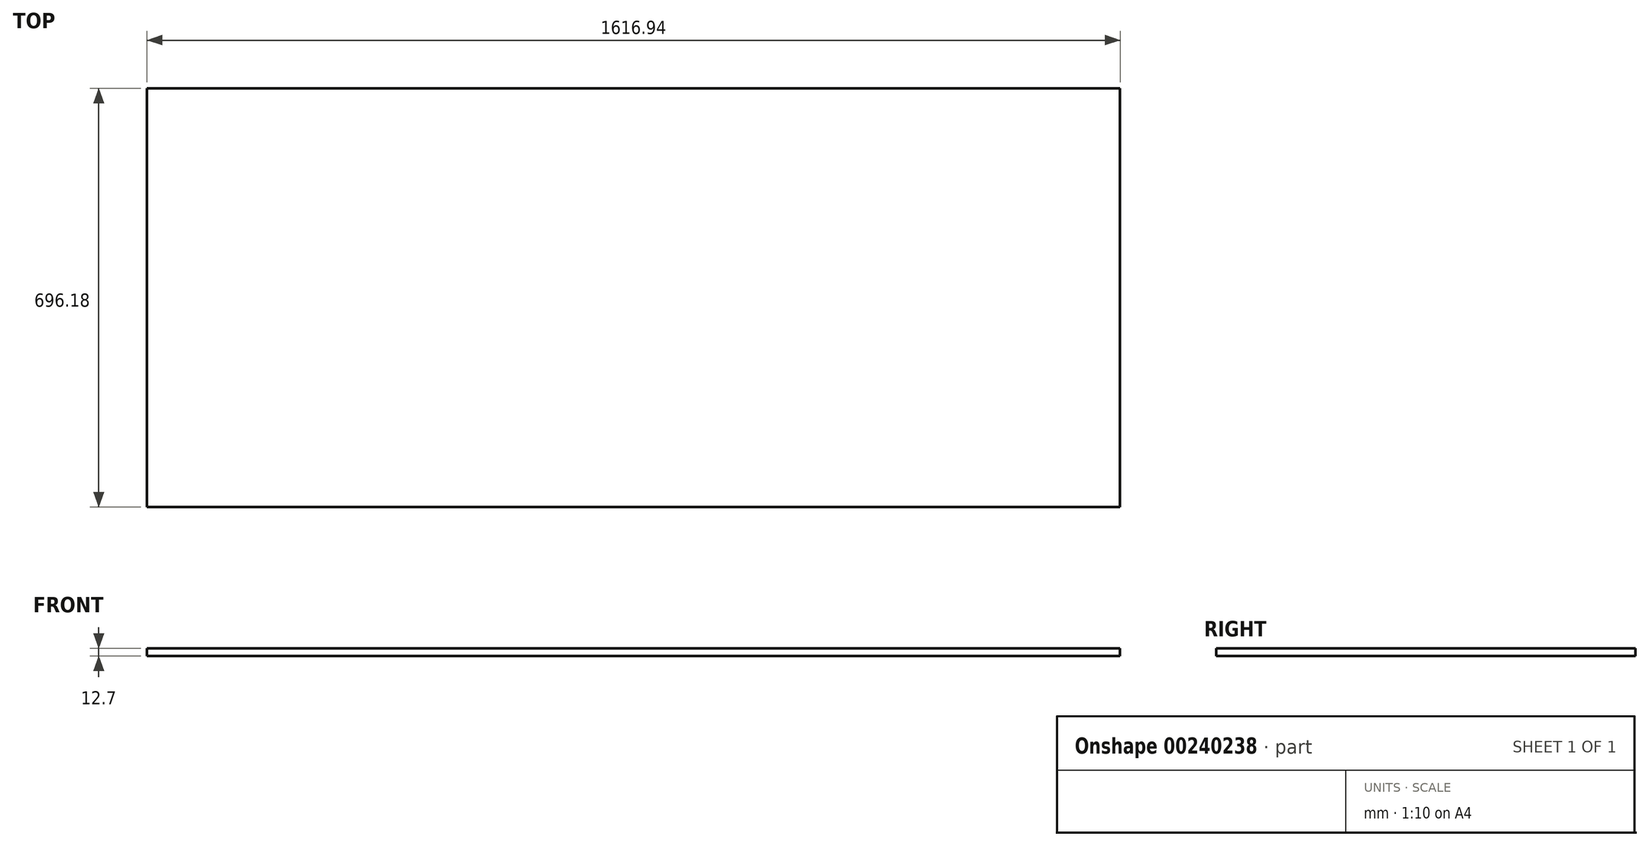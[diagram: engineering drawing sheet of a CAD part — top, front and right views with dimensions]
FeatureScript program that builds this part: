
annotation { "Feature Type Name" : "Feature", "Feature Type Description" : "" }
export const myFeature = defineFeature(function(context is Context, id is Id, definition is map)
    precondition{}
    {
        {
            var Q0;
            Q0=qCreatedBy(makeId("Top.planeOp"),FACE);
            var sketch = newSketch(context, id + "F0", { "sketchPlane" : qUnion([Q0])});
            skLineSegment(sketch, "E0.bottom", {"start": v(808.47, -348.1) * mm, "end": v(-808.47, -348.1) * mm});
            skLineSegment(sketch, "E0.top", {"start": v(808.47, 348.1) * mm, "end": v(-808.47, 348.1) * mm});
            skLineSegment(sketch, "E0.left", {"start": v(808.47, -348.1) * mm, "end": v(808.47, 348.1) * mm});
            skLineSegment(sketch, "E0.right", {"start": v(-808.47, -348.1) * mm, "end": v(-808.47, 348.1) * mm});
            skPoint(sketch, "E0.middle", {"position": v(0, 0) * mm});
            skLineSegment(sketch, "E1", {"start": v(0, 348.1) * mm, "end": v(0, -348.1) * mm, "construction": true});
            skLineSegment(sketch, "E2", {"start": v(-808.47, 0) * mm, "end": v(808.47, 0) * mm, "construction": true});
            skLineSegment(sketch, "E3.bottom", {"start": v(76.2, -76.2) * mm, "end": v(-76.2, -76.2) * mm, "construction": true});
            skLineSegment(sketch, "E3.top", {"start": v(76.2, 76.2) * mm, "end": v(-76.2, 76.2) * mm, "construction": true});
            skLineSegment(sketch, "E3.left", {"start": v(76.2, -76.2) * mm, "end": v(76.2, 76.2) * mm, "construction": true});
            skLineSegment(sketch, "E3.right", {"start": v(-76.2, -76.2) * mm, "end": v(-76.2, 76.2) * mm, "construction": true});
            skLineSegment(sketch, "E4.bottom", {"start": v(-82.55, -82.55) * mm, "end": v(82.55, -82.55) * mm, "construction": true});
            skLineSegment(sketch, "E4.top", {"start": v(-82.55, 82.55) * mm, "end": v(82.55, 82.55) * mm, "construction": true});
            skLineSegment(sketch, "E4.left", {"start": v(-82.55, -82.55) * mm, "end": v(-82.55, 82.55) * mm, "construction": true});
            skLineSegment(sketch, "E4.right", {"start": v(82.55, -82.55) * mm, "end": v(82.55, 82.55) * mm, "construction": true});
            skLineSegment(sketch, "E5.bottom", {"start": v(76.2, 82.55) * mm, "end": v(-228.6, 82.55) * mm, "construction": true});
            skLineSegment(sketch, "E5.left", {"start": v(76.2, 82.55) * mm, "end": v(76.2, 341.74) * mm, "construction": true});
            skLineSegment(sketch, "E5.right", {"start": v(-228.6, 82.55) * mm, "end": v(-228.6, 348.1) * mm, "construction": true});
            skPoint(sketch, "E5.middle", {"position": v(-76.2, 234.95) * mm});
            skLineSegment(sketch, "E6", {"start": v(-76.2, 348.1) * mm, "end": v(-76.2, -348.1) * mm, "construction": true});
            skLineSegment(sketch, "E7.0", {"start": v(-381, 341.74) * mm, "end": v(-381, -341.74) * mm, "construction": true});
            skLineSegment(sketch, "E8.0", {"start": v(76.2, 341.74) * mm, "end": v(76.2, -341.74) * mm, "construction": true});
            skLineSegment(sketch, "E9.bottom", {"start": v(228.6, -387.35) * mm, "end": v(-76.2, -387.35) * mm, "construction": true});
            skLineSegment(sketch, "E9.top", {"start": v(228.6, -82.55) * mm, "end": v(-76.2, -82.55) * mm, "construction": true});
            skLineSegment(sketch, "E9.left", {"start": v(228.6, -387.35) * mm, "end": v(228.6, -82.55) * mm, "construction": true});
            skLineSegment(sketch, "E9.right", {"start": v(-76.2, -387.35) * mm, "end": v(-76.2, -82.55) * mm, "construction": true});
            skPoint(sketch, "E9.middle", {"position": v(76.2, -234.95) * mm});
            skLineSegment(sketch, "E10.bottom", {"start": v(387.35, -76.2) * mm, "end": v(82.55, -76.2) * mm, "construction": true});
            skLineSegment(sketch, "E10.top", {"start": v(387.35, 228.6) * mm, "end": v(82.55, 228.6) * mm, "construction": true});
            skLineSegment(sketch, "E10.left", {"start": v(387.35, -76.2) * mm, "end": v(387.35, 228.6) * mm, "construction": true});
            skLineSegment(sketch, "E10.right", {"start": v(82.55, -76.2) * mm, "end": v(82.55, 228.6) * mm, "construction": true});
            skPoint(sketch, "E10.middle", {"position": v(234.95, 76.2) * mm});
            skLineSegment(sketch, "E11.0", {"start": v(-805.3, -76.2) * mm, "end": v(805.3, -76.2) * mm, "construction": true});
            skLineSegment(sketch, "E12.0", {"start": v(-805.3, 76.2) * mm, "end": v(805.3, 76.2) * mm, "construction": true});
            skLineSegment(sketch, "E13.bottom", {"start": v(-82.55, -228.6) * mm, "end": v(-387.35, -228.6) * mm, "construction": true});
            skLineSegment(sketch, "E13.top", {"start": v(-82.55, 76.2) * mm, "end": v(-387.35, 76.2) * mm, "construction": true});
            skLineSegment(sketch, "E13.left", {"start": v(-82.55, -228.6) * mm, "end": v(-82.55, 76.2) * mm, "construction": true});
            skLineSegment(sketch, "E13.right", {"start": v(-387.35, -228.6) * mm, "end": v(-387.35, 76.2) * mm, "construction": true});
            skPoint(sketch, "E13.middle", {"position": v(-234.95, -76.2) * mm});
            skSolve(sketch);
        }
        {
            var Q0;
            Q0=makeQuery(id+"F0.imprint","IMPRINT",FACE,{"disambiguationData":[TD([[makeQuery(id+"F0.imprint","IMPRINT",EDGE,{"derivedFrom":sQuery(id+"F0.wireOp",EDGE,"E0.bottom")}),-1.0]])]});
            extrude(context, id + "F1", {"entities" : qUnion([Q0]), "endBound" : BoundingType.SYMMETRIC, "depth" : 12.7 * mm});
        }
    });
